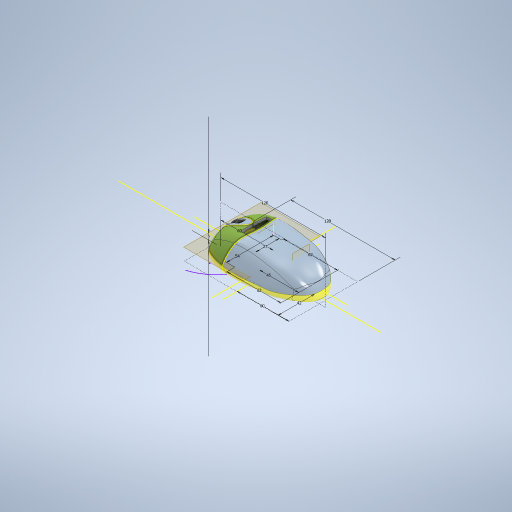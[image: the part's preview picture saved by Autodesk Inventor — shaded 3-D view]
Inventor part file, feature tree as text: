
AUTODESK INVENTOR PART (.ipt)
format: ipt  version: 2024 (Build 280153000, 153)  size: 4,726,272 bytes
history: native  units: mm
features: other x31, sketch x22, extrude x13, split x12, plane x7, surface_op x7, fillet x4, thicken_offset x2, shell x1, sweep x1, hole x1
ambient origin geometry x8: Origin, YZ Plane, XZ Plane, XY Plane, X Axis, Y Axis, Z Axis, Center Point
bodies: Solid2 (feature_tree), Solid3 (feature_tree), Solid4 (feature_tree), Solid5 (feature_tree), Solid6 (feature_tree)
feature tree (101):
  other  "CrossSection1"
  other  "Curvature1"
  other  "Curvature2"
  other  "Curvature3"
  other  "Curvature4"
  other  "Curvature5"
  sketch  "Sketch1"  dims[d1=7.0mm d2=60.0mm d3=120.0mm d5=120.0mm d9=42.0mm d10=60.0mm]
  sketch  "Sketch2"  dims[d13=0.5mm d14=2.0mm d15=0.0mm d16=20.0mm d21=1.0mm]
  other  "Form2"
  extrude  "Extrusion2"  Depth=60.0mm
  sketch  "Sketch5"  dims[d37=3.0mm d38=3.0mm d39=10.0mm d40=0.0mm]
  sketch  "3D Sketch1"
  split  "Split1"
  split  "Split6"
  split  "Split7"
  split  "Split8"
  plane  "Work Plane2"
  split  "Split9"
  other  "Ruled Surface1"
  surface_op  "Extend1"
  other  "Ruled Surface2"
  surface_op  "Extend2"
  other  "Ruled Surface3"
  surface_op  "Extend3"
  surface_op  "Stitch Surface1"
  other  "Ruled Surface4"
  surface_op  "Extend5"
  surface_op  "Stitch Surface4"
  split  "Split10"
  shell  "Shell1"  Thickness=120.0mm
  split  "Split11"
  surface_op  "Extend6"
  split  "Split12"
  split  "Split13"
  split  "Split14"
  fillet  "Fillet1"  Radius=120.0mm
  fillet  "Fillet2"  Radius=42.0mm
  fillet  "Fillet3"  Radius=60.0mm
  plane  "Work Plane3"
  plane  "Work Plane4"
  split  "Split15"
  split  "Split16"
  sweep  "Sweep1"
  extrude  "Extrusion3"  Depth=8.0mm
  extrude  "Extrusion4"  Depth=10.0mm TaperAngle=0.0deg
  extrude  "Extrusion5"  Depth=10.0mm TaperAngle=0.0deg
  thicken_offset  "Thicken3"
  thicken_offset  "Thicken4"
  extrude  "Extrusion6"  Depth=10.0mm TaperAngle=0.0deg
  fillet  "Fillet4"  Radius=3.0mm
  hole  "Hole1"  [1 undecoded]
  plane  "Work Plane5"
  extrude  "Extrusion7"  Depth=3.0mm
  extrude  "Extrusion8"  Depth=4.0mm
  extrude  "Extrusion9"  Depth=100.0mm TaperAngle=0.0deg
  other  "Snap Fit1"
  plane  "Work Plane6"
  plane  "Work Plane7"
  other  "Lip2"
  other  "Lip3"
  sketch  "Sketch22"  dims[d82=1.3mm]
  other  "Boss1"
  other  "Boss2"
  extrude  "Extrusion10"  Depth=1.0mm
  plane  "Work Plane8"
  extrude  "Extrusion11"  Depth=1.0mm
  extrude  "Extrusion12"  Depth=40.0mm TaperAngle=0.0deg
  other  "Image1"
  other  "Image2"
  sketch  "Sketch4"  dims[d22=10.0mm d23=0.0mm d36=8.0mm]
  other  "Project to Surface1"
  other  "Srf1"
  other  "Srf2"
  other  "Srf3"
  other  "Srf4"
  other  "Srf5"
  other  "Srf6"
  other  "Srf9"
  other  "Srf10"
  sketch  "Sketch7"  dims[d41=3.0mm d42=10.0mm d43=0.0mm]
  other  "Srf11"
  sketch  "Sketch10"  dims[d44=3.0mm d45=10.0mm d46=0.0mm d47=3.0mm]
  other  "Srf12"
  sketch  "3D Sketch2"
  sketch  "Sketch11"  dims[d48=10.0mm d49=0.0mm d51=3.0mm]
  sketch  "Sketch12"  dims[d52=1.0mm d53=3.0mm]
  sketch  "Sketch13"  dims[d54=3.0mm d55=4.0mm]
  sketch  "Sketch14"  dims[d56=1.0mm d57=100.0mm d58=0.0mm]
  sketch  "Sketch15"  dims[d69=1.0mm d70=1.0mm]
  sketch  "Sketch16"  dims[d71=1.0mm d72=1.0mm]
  sketch  "Sketch18"  dims[d73=1.0mm d74=40.0mm d75=0.0mm]
  sketch  "Sketch19"  dims[d76=1.0mm d77=1.0mm]
  sketch  "Sketch20"  dims[d78=1.0mm d79=14.0mm d80=-14.0mm]
  sketch  "Sketch21"  dims[d81=14.0mm]
  sketch  "Sketch25"  dims[d83=0.0mm d84=0.0mm]
  sketch  "Sketch29"  dims[d85=1.0mm]
  sketch  "Sketch30"  dims[d86=1.0mm d87=20.0mm d88=2.3mm d89=25.0mm d90=0.0mm d91=20.0mm d92=6.0mm d93=3.0mm d94=5.0mm d95=1.3mm d96=0.0mm d97=1.0mm d98=0.5mm d99=30.0mm d100=19.0mm d101=20.0mm d102=0.0mm d103=1.0mm d104=1.0mm d105=1.0mm d106=1.0mm d107=27.0mm d108=48.0mm d109=30.0mm d110=8.0mm d111=-4.363323mm d112=4.0mm d113=4.0mm d114=4.0mm d115=9.0mm d116=9.0mm d117=2.0mm d118=6.0mm d119=4.0mm d120=2.0mm d121=90.0deg d122=15.0mm d123=20.594885mm d124=0.0mm d127=2.5mm d128=2.5mm d129=8.0mm d130=0.0mm d131=1.5mm d132=1.5mm d133=1.5mm d134=0.0mm d135=17.0mm d136=4.0mm d137=1.3mm d138=1.5mm d139=0.0mm d140=7.0mm d141=8.5mm d142=1.35mm d143=1.2mm d144=0.7mm d145=0.7mm d146=3.0mm d147=3.0mm d148=0.5mm d149=0.5mm d150=12.217305mm d151=3.490659mm d152=35.0mm d153=4.0mm d160=1.0mm d161=0.65mm d162=0.0mm d163=0.0mm d164=0.0mm d165=0.0mm d166=1.0mm d167=0.65mm d168=0.0mm d169=0.0mm d170=0.0mm d171=0.0mm d172=54.0mm d173=27.0mm d174=62.0mm d175=62.0mm d176=45.0mm d177=0.3mm d178=0.0mm d179=4.0mm d180=1.3mm d181=0.5mm d182=3.0mm d183=1.25mm d184=2.2mm d185=0.0mm d186=0.0mm d187=0.0mm d188=0.0mm d189=90.0deg d190=20.0mm d192=2.0mm d193=2.0mm d194=10.0mm d195=0.0mm d196=1.745329mm d197=0.436332mm d198=0.0mm d199=0.0mm d200=0.0mm d201=360.0deg d202=0.5mm d203=0.0mm d204=3.0mm d205=1.0mm d206=10.0mm d207=0.174533mm d208=0.174533mm d209=20.0mm d211=2.0mm d212=2.0mm d213=10.0mm d214=0.0mm d215=1.745329mm d216=0.436332mm d217=0.0mm d218=0.0mm d219=0.0mm d220=360.0deg d221=0.8mm d222=6.0mm d223=20.0mm d224=0.0mm d225=-12.0mm d232=2.0mm d233=2.0mm d234=39.0mm d235=39.0mm d236=3.0mm d237=3.0mm d238=13.0mm d239=0.0mm d240=1.2mm d241=3.4mm d242=1.3mm d243=3.0mm d244=0.0mm]
  other  "OffsetSrf1"
  other  "OffsetSrf2"
  extrude  "ExtrusionSrf1"  Depth=1.0mm
  extrude  "ExtrusionSrf2"  Depth=14.0mm
note: 1 required parameter value undecoded (feature->parameter linkage not recoverable at this tier; creation-order binding heuristic only, values carry confidence <= 0.55)
